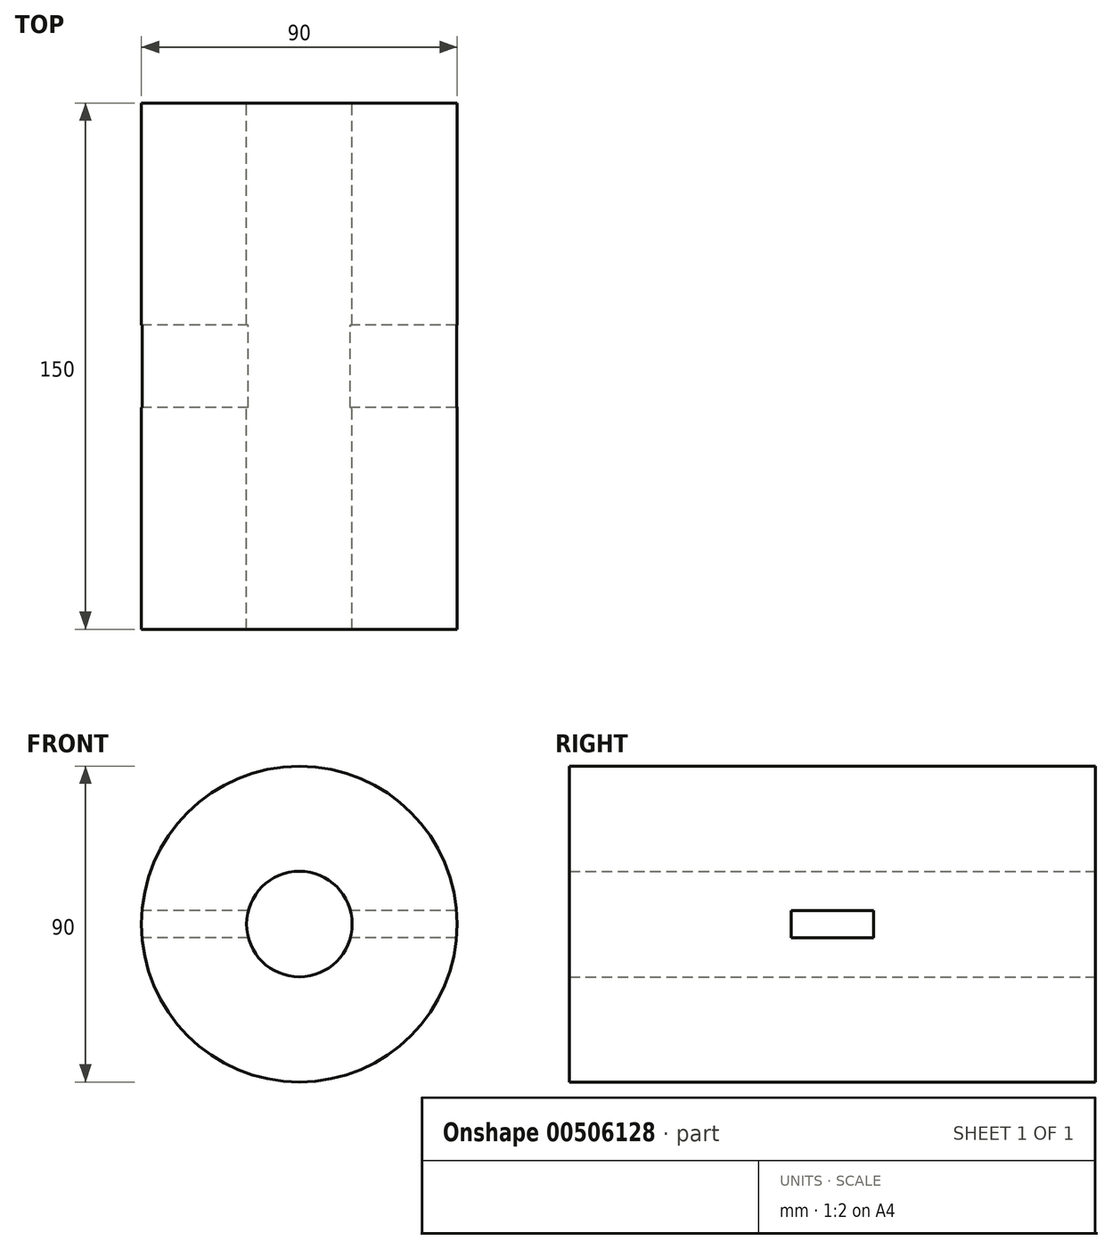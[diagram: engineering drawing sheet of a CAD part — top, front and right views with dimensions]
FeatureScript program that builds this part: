
annotation { "Feature Type Name" : "Feature", "Feature Type Description" : "" }
export const myFeature = defineFeature(function(context is Context, id is Id, definition is map)
    precondition{}
    {
        {
            var Q0;
            Q0=qCreatedBy(makeId("Front.planeOp"),FACE);
            var sketch = newSketch(context, id + "F0", { "sketchPlane" : qUnion([Q0])});
            skCircle(sketch, "E0", {"center": v(0, 0) * mm, "radius": 45 * mm});
            skSolve(sketch);
        }
        {
            var Q0;
            Q0=makeQuery(id+"F0.imprint","IMPRINT",FACE,{"disambiguationData":[TD([[makeQuery(id+"F0.imprint","IMPRINT",EDGE,{"derivedFrom":sQuery(id+"F0.wireOp",EDGE,"E0")}),1.0]])]});
            extrude(context, id + "F1", {"entities" : qUnion([Q0]), "endBound" : BoundingType.SYMMETRIC, "depth" : 150 * mm});
        }
        {
            var Q0;
            Q0=makeQuery(id+"F1.opExtrude","CAP_FACE",FACE,{"disambiguationData":[OSD([sQuery(id+"F0.wireOp",EDGE,"E0")])],"isStart":false});
            var sketch = newSketch(context, id + "F2", { "sketchPlane" : qUnion([Q0])});
            skCircle(sketch, "E1", {"center": v(0, 0) * mm, "radius": 15.05 * mm});
            skSolve(sketch);
        }
        {
            var Q0;
            Q0=makeQuery(id+"F2.imprint","IMPRINT",FACE,{"disambiguationData":[TD([[makeQuery(id+"F2.imprint","IMPRINT",EDGE,{"derivedFrom":sQuery(id+"F2.wireOp",EDGE,"E1")}),1.0]])]});
            extrude(context, id + "F3", {"entities" : qUnion([Q0]), "operationType" : NewBodyOperationType.REMOVE, "endBound" : BoundingType.SYMMETRIC, "depth" : 300 * mm});
        }
        {
            var Q0;
            Q0=qCreatedBy(makeId("Right.planeOp"),FACE);
            var sketch = newSketch(context, id + "F4", { "sketchPlane" : qUnion([Q0])});
            skLineSegment(sketch, "E2.bottom", {"start": v(-11.75, -3.9) * mm, "end": v(11.75, -3.9) * mm});
            skLineSegment(sketch, "E2.top", {"start": v(-11.75, 3.9) * mm, "end": v(11.75, 3.9) * mm});
            skLineSegment(sketch, "E2.left", {"start": v(-11.75, -3.9) * mm, "end": v(-11.75, 3.9) * mm});
            skLineSegment(sketch, "E2.right", {"start": v(11.75, -3.9) * mm, "end": v(11.75, 3.9) * mm});
            skPoint(sketch, "E2.middle", {"position": v(0, 0) * mm});
            skSolve(sketch);
        }
        {
            var Q0;
            Q0=makeQuery(id+"F4.imprint","IMPRINT",FACE,{"disambiguationData":[TD([[makeQuery(id+"F4.imprint","IMPRINT",EDGE,{"derivedFrom":sQuery(id+"F4.wireOp",EDGE,"E2.bottom")}),1.0]])]});
            extrude(context, id + "F5", {"entities" : qUnion([Q0]), "operationType" : NewBodyOperationType.REMOVE, "endBound" : BoundingType.SYMMETRIC, "depth" : 126 * mm});
        }
    });
